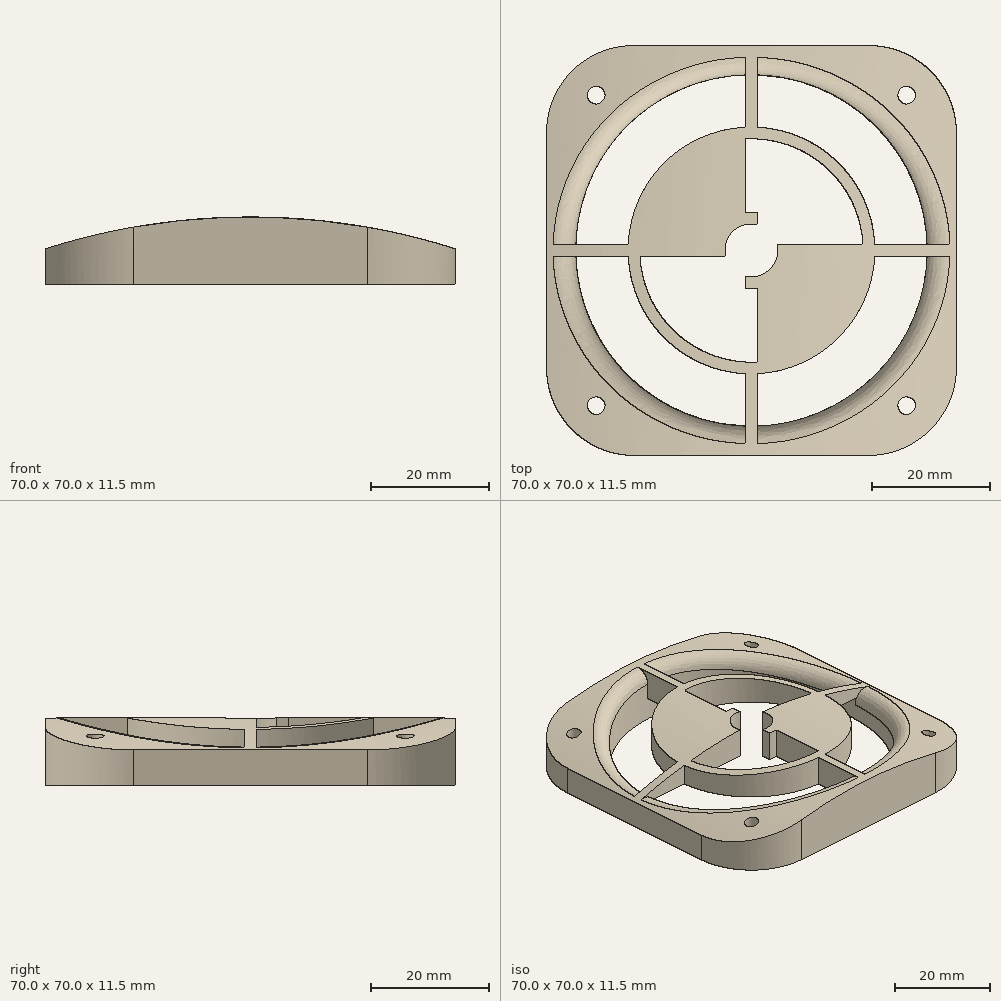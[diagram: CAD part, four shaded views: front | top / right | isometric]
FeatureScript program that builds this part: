
annotation { "Feature Type Name" : "Feature", "Feature Type Description" : "" }
export const myFeature = defineFeature(function(context is Context, id is Id, definition is map)
    precondition{}
    {
        {
            var Q0;
            Q0=qCreatedBy(makeId("Top.planeOp"),FACE);
            var sketch = newSketch(context, id + "F0", { "sketchPlane" : qUnion([Q0])});
            skLineSegment(sketch, "E0", {"start": v(0, 70.57) * mm, "end": v(0, -91.76) * mm, "construction": true});
            skLineSegment(sketch, "E1", {"start": v(-109.37, 0) * mm, "end": v(112.01, 0) * mm, "construction": true});
            skCircle(sketch, "E2", {"center": v(0, 0) * mm, "radius": 30 * mm});
            skLineSegment(sketch, "E3.bottom", {"start": v(35, 35) * mm, "end": v(-35, 35) * mm});
            skLineSegment(sketch, "E3.top", {"start": v(35, -35) * mm, "end": v(-35, -35) * mm});
            skLineSegment(sketch, "E3.left", {"start": v(35, 35) * mm, "end": v(35, -35) * mm});
            skLineSegment(sketch, "E3.right", {"start": v(-35, 35) * mm, "end": v(-35, -35) * mm});
            skLineSegment(sketch, "E4.bottom", {"start": v(26.5, 26.5) * mm, "end": v(-26.5, 26.5) * mm, "construction": true});
            skLineSegment(sketch, "E4.top", {"start": v(26.5, -26.5) * mm, "end": v(-26.5, -26.5) * mm, "construction": true});
            skLineSegment(sketch, "E4.left", {"start": v(26.5, 26.5) * mm, "end": v(26.5, -26.5) * mm, "construction": true});
            skLineSegment(sketch, "E4.right", {"start": v(-26.5, 26.5) * mm, "end": v(-26.5, -26.5) * mm, "construction": true});
            skCircle(sketch, "E5", {"center": v(26.5, 26.5) * mm, "radius": 1.5 * mm});
            skCircle(sketch, "E6.MirrorC", {"center": v(-26.5, 26.5) * mm, "radius": 1.5 * mm});
            skCircle(sketch, "E7.MirrorC", {"center": v(26.5, -26.5) * mm, "radius": 1.5 * mm});
            skCircle(sketch, "E8.MirrorC", {"center": v(-26.5, -26.5) * mm, "radius": 1.5 * mm});
            skCircle(sketch, "E9", {"center": v(0, 0) * mm, "radius": 6.52 * mm});
            skCircle(sketch, "E10.0", {"center": v(0, 0) * mm, "radius": 4.52 * mm});
            skCircle(sketch, "E11", {"center": v(0, 0) * mm, "radius": 19.07 * mm});
            skCircle(sketch, "E12.0", {"center": v(0, 0) * mm, "radius": 21.07 * mm});
            skLineSegment(sketch, "E13", {"start": v(-29.98, -1) * mm, "end": v(29.98, -1) * mm});
            skLineSegment(sketch, "E14.MirrorCS", {"start": v(-29.98, 1) * mm, "end": v(29.98, 1) * mm});
            skLineSegment(sketch, "E15", {"start": v(1, 29.98) * mm, "end": v(1, -29.98) * mm});
            skLineSegment(sketch, "E16.MirrorCS", {"start": v(-1, 29.98) * mm, "end": v(-1, -29.98) * mm});
            skSolve(sketch);
        }
        {
            var Q0;
            Q0=qSketchRegion(id+"F0",true);
            var Q1;
            {var subQ0=sQuery(id+"F0.wireOp",EDGE,"E16.MirrorCS");var subQ1=sQuery(id+"F0.wireOp",EDGE,"E11");var subQ2=makeQuery(id+"F0.imprint","INTERSECT",VERTEX,{"disambiguationData":[OD(0.0)],"derivedFrom":[subQ1,subQ0]});Q1=makeQuery(id+"F0.imprint","IMPRINT",FACE,{"disambiguationData":[TD([[makeQuery(id+"F0.imprint","IMPRINT",EDGE,{"disambiguationData":[TD([[subQ2,-1.0]])],"derivedFrom":subQ1}),-1.0]])]});}
            var Q2;
            {var subQ0=sQuery(id+"F0.wireOp",EDGE,"E13");var subQ1=sQuery(id+"F0.wireOp",EDGE,"E2");var subQ2=makeQuery(id+"F0.imprint","INTERSECT",VERTEX,{"disambiguationData":[OD(0.0)],"derivedFrom":[subQ1,subQ0]});Q2=makeQuery(id+"F0.imprint","IMPRINT",FACE,{"disambiguationData":[TD([[makeQuery(id+"F0.imprint","IMPRINT",EDGE,{"disambiguationData":[TD([[subQ2,1.0]])],"derivedFrom":subQ1}),1.0]])]});}
            var Q3;
            {var subQ0=sQuery(id+"F0.wireOp",EDGE,"E13");var subQ1=sQuery(id+"F0.wireOp",EDGE,"E11");var subQ2=makeQuery(id+"F0.imprint","INTERSECT",VERTEX,{"disambiguationData":[OD(0.0)],"derivedFrom":[subQ1,subQ0]});Q3=makeQuery(id+"F0.imprint","IMPRINT",FACE,{"disambiguationData":[TD([[makeQuery(id+"F0.imprint","IMPRINT",EDGE,{"disambiguationData":[TD([[subQ2,-1.0]])],"derivedFrom":subQ1}),-1.0]])]});}
            var Q4;
            {var subQ0=sQuery(id+"F0.wireOp",EDGE,"E14.MirrorCS");var subQ1=sQuery(id+"F0.wireOp",EDGE,"E9");var subQ2=makeQuery(id+"F0.imprint","INTERSECT",VERTEX,{"disambiguationData":[OD(1.0)],"derivedFrom":[subQ1,subQ0]});Q4=makeQuery(id+"F0.imprint","IMPRINT",FACE,{"disambiguationData":[TD([[makeQuery(id+"F0.imprint","IMPRINT",EDGE,{"disambiguationData":[TD([[subQ2,-1.0]])],"derivedFrom":subQ1}),-1.0]])]});}
            var Q5;
            {var subQ0=sQuery(id+"F0.wireOp",EDGE,"E14.MirrorCS");var subQ1=sQuery(id+"F0.wireOp",EDGE,"E11");var subQ2=makeQuery(id+"F0.imprint","INTERSECT",VERTEX,{"disambiguationData":[OD(1.0)],"derivedFrom":[subQ1,subQ0]});Q5=makeQuery(id+"F0.imprint","IMPRINT",FACE,{"disambiguationData":[TD([[makeQuery(id+"F0.imprint","IMPRINT",EDGE,{"disambiguationData":[TD([[subQ2,-1.0]])],"derivedFrom":subQ1}),-1.0]])]});}
            var Q6;
            {var subQ0=sQuery(id+"F0.wireOp",EDGE,"E13");var subQ1=sQuery(id+"F0.wireOp",EDGE,"E9");var subQ2=makeQuery(id+"F0.imprint","INTERSECT",VERTEX,{"disambiguationData":[OD(0.0)],"derivedFrom":[subQ1,subQ0]});Q6=makeQuery(id+"F0.imprint","IMPRINT",FACE,{"disambiguationData":[TD([[makeQuery(id+"F0.imprint","IMPRINT",EDGE,{"disambiguationData":[TD([[subQ2,-1.0]])],"derivedFrom":subQ1}),1.0]])]});}
            var Q7;
            {var subQ0=sQuery(id+"F0.wireOp",EDGE,"E14.MirrorCS");var subQ1=sQuery(id+"F0.wireOp",EDGE,"E9");var subQ2=makeQuery(id+"F0.imprint","INTERSECT",VERTEX,{"disambiguationData":[OD(1.0)],"derivedFrom":[subQ1,subQ0]});Q7=makeQuery(id+"F0.imprint","IMPRINT",FACE,{"disambiguationData":[TD([[makeQuery(id+"F0.imprint","IMPRINT",EDGE,{"disambiguationData":[TD([[subQ2,-1.0]])],"derivedFrom":subQ1}),1.0]])]});}
            var Q8;
            {var subQ0=sQuery(id+"F0.wireOp",EDGE,"E16.MirrorCS");var subQ1=sQuery(id+"F0.wireOp",EDGE,"E9");var subQ2=makeQuery(id+"F0.imprint","INTERSECT",VERTEX,{"disambiguationData":[OD(0.0)],"derivedFrom":[subQ1,subQ0]});Q8=makeQuery(id+"F0.imprint","IMPRINT",FACE,{"disambiguationData":[TD([[makeQuery(id+"F0.imprint","IMPRINT",EDGE,{"disambiguationData":[TD([[subQ2,-1.0]])],"derivedFrom":subQ1}),1.0]])]});}
            var Q9;
            {var subQ0=sQuery(id+"F0.wireOp",EDGE,"E15");var subQ1=sQuery(id+"F0.wireOp",EDGE,"E9");var subQ2=makeQuery(id+"F0.imprint","INTERSECT",VERTEX,{"disambiguationData":[OD(0.0)],"derivedFrom":[subQ1,subQ0]});Q9=makeQuery(id+"F0.imprint","IMPRINT",FACE,{"disambiguationData":[TD([[makeQuery(id+"F0.imprint","IMPRINT",EDGE,{"disambiguationData":[TD([[subQ2,-1.0]])],"derivedFrom":subQ1}),1.0]])]});}
            var Q10;
            {var subQ0=sQuery(id+"F0.wireOp",EDGE,"E15");var subQ1=sQuery(id+"F0.wireOp",EDGE,"E9");var subQ2=makeQuery(id+"F0.imprint","INTERSECT",VERTEX,{"disambiguationData":[OD(0.0)],"derivedFrom":[subQ1,subQ0]});Q10=makeQuery(id+"F0.imprint","IMPRINT",FACE,{"disambiguationData":[TD([[makeQuery(id+"F0.imprint","IMPRINT",EDGE,{"disambiguationData":[TD([[subQ2,1.0]])],"derivedFrom":subQ1}),1.0]])]});}
            var Q11;
            {var subQ0=sQuery(id+"F0.wireOp",EDGE,"E14.MirrorCS");var subQ1=sQuery(id+"F0.wireOp",EDGE,"E9");var subQ2=makeQuery(id+"F0.imprint","INTERSECT",VERTEX,{"disambiguationData":[OD(0.0)],"derivedFrom":[subQ1,subQ0]});Q11=makeQuery(id+"F0.imprint","IMPRINT",FACE,{"disambiguationData":[TD([[makeQuery(id+"F0.imprint","IMPRINT",EDGE,{"disambiguationData":[TD([[subQ2,1.0]])],"derivedFrom":subQ1}),1.0]])]});}
            var Q12;
            {var subQ0=sQuery(id+"F0.wireOp",EDGE,"E15");var subQ1=sQuery(id+"F0.wireOp",EDGE,"E9");var subQ2=makeQuery(id+"F0.imprint","INTERSECT",VERTEX,{"disambiguationData":[OD(1.0)],"derivedFrom":[subQ1,subQ0]});Q12=makeQuery(id+"F0.imprint","IMPRINT",FACE,{"disambiguationData":[TD([[makeQuery(id+"F0.imprint","IMPRINT",EDGE,{"disambiguationData":[TD([[subQ2,-1.0]])],"derivedFrom":subQ1}),1.0]])]});}
            var Q13;
            {var subQ0=sQuery(id+"F0.wireOp",EDGE,"E16.MirrorCS");var subQ1=sQuery(id+"F0.wireOp",EDGE,"E11");var subQ2=makeQuery(id+"F0.imprint","INTERSECT",VERTEX,{"disambiguationData":[OD(1.0)],"derivedFrom":[subQ1,subQ0]});Q13=makeQuery(id+"F0.imprint","IMPRINT",FACE,{"disambiguationData":[TD([[makeQuery(id+"F0.imprint","IMPRINT",EDGE,{"disambiguationData":[TD([[subQ2,-1.0]])],"derivedFrom":subQ1}),-1.0]])]});}
            var Q14;
            {var subQ0=sQuery(id+"F0.wireOp",EDGE,"E15");var subQ1=sQuery(id+"F0.wireOp",EDGE,"E2");var subQ2=makeQuery(id+"F0.imprint","INTERSECT",VERTEX,{"disambiguationData":[OD(1.0)],"derivedFrom":[subQ1,subQ0]});Q14=makeQuery(id+"F0.imprint","IMPRINT",FACE,{"disambiguationData":[TD([[makeQuery(id+"F0.imprint","IMPRINT",EDGE,{"disambiguationData":[TD([[subQ2,1.0]])],"derivedFrom":subQ1}),1.0]])]});}
            var Q15;
            {var subQ0=sQuery(id+"F0.wireOp",EDGE,"E16.MirrorCS");var subQ1=sQuery(id+"F0.wireOp",EDGE,"E9");var subQ2=makeQuery(id+"F0.imprint","INTERSECT",VERTEX,{"disambiguationData":[OD(1.0)],"derivedFrom":[subQ1,subQ0]});Q15=makeQuery(id+"F0.imprint","IMPRINT",FACE,{"disambiguationData":[TD([[makeQuery(id+"F0.imprint","IMPRINT",EDGE,{"disambiguationData":[TD([[subQ2,-1.0]])],"derivedFrom":subQ1}),-1.0]])]});}
            var Q16;
            {var subQ0=sQuery(id+"F0.wireOp",EDGE,"E15");var subQ1=sQuery(id+"F0.wireOp",EDGE,"E11");var subQ2=makeQuery(id+"F0.imprint","INTERSECT",VERTEX,{"disambiguationData":[OD(1.0)],"derivedFrom":[subQ1,subQ0]});Q16=makeQuery(id+"F0.imprint","IMPRINT",FACE,{"disambiguationData":[TD([[makeQuery(id+"F0.imprint","IMPRINT",EDGE,{"disambiguationData":[TD([[subQ2,-1.0]])],"derivedFrom":subQ1}),-1.0]])]});}
            var Q17;
            {var subQ0=sQuery(id+"F0.wireOp",EDGE,"E14.MirrorCS");var subQ1=sQuery(id+"F0.wireOp",EDGE,"E11");var subQ2=makeQuery(id+"F0.imprint","INTERSECT",VERTEX,{"disambiguationData":[OD(0.0)],"derivedFrom":[subQ1,subQ0]});Q17=makeQuery(id+"F0.imprint","IMPRINT",FACE,{"disambiguationData":[TD([[makeQuery(id+"F0.imprint","IMPRINT",EDGE,{"disambiguationData":[TD([[subQ2,1.0]])],"derivedFrom":subQ1}),-1.0]])]});}
            var Q18;
            {var subQ0=sQuery(id+"F0.wireOp",EDGE,"E14.MirrorCS");var subQ1=sQuery(id+"F0.wireOp",EDGE,"E9");var subQ2=makeQuery(id+"F0.imprint","INTERSECT",VERTEX,{"disambiguationData":[OD(0.0)],"derivedFrom":[subQ1,subQ0]});Q18=makeQuery(id+"F0.imprint","IMPRINT",FACE,{"disambiguationData":[TD([[makeQuery(id+"F0.imprint","IMPRINT",EDGE,{"disambiguationData":[TD([[subQ2,1.0]])],"derivedFrom":subQ1}),-1.0]])]});}
            var Q19;
            {var subQ0=sQuery(id+"F0.wireOp",EDGE,"E15");var subQ1=sQuery(id+"F0.wireOp",EDGE,"E11");var subQ2=makeQuery(id+"F0.imprint","INTERSECT",VERTEX,{"disambiguationData":[OD(0.0)],"derivedFrom":[subQ1,subQ0]});Q19=makeQuery(id+"F0.imprint","IMPRINT",FACE,{"disambiguationData":[TD([[makeQuery(id+"F0.imprint","IMPRINT",EDGE,{"disambiguationData":[TD([[subQ2,1.0]])],"derivedFrom":subQ1}),-1.0]])]});}
            var Q20;
            {var subQ0=sQuery(id+"F0.wireOp",EDGE,"E15");var subQ1=sQuery(id+"F0.wireOp",EDGE,"E11");var subQ2=makeQuery(id+"F0.imprint","INTERSECT",VERTEX,{"disambiguationData":[OD(0.0)],"derivedFrom":[subQ1,subQ0]});Q20=makeQuery(id+"F0.imprint","IMPRINT",FACE,{"disambiguationData":[TD([[makeQuery(id+"F0.imprint","IMPRINT",EDGE,{"disambiguationData":[TD([[subQ2,-1.0]])],"derivedFrom":subQ1}),-1.0]])]});}
            var Q21;
            {var subQ0=sQuery(id+"F0.wireOp",EDGE,"E15");var subQ1=sQuery(id+"F0.wireOp",EDGE,"E2");var subQ2=makeQuery(id+"F0.imprint","INTERSECT",VERTEX,{"disambiguationData":[OD(0.0)],"derivedFrom":[subQ1,subQ0]});Q21=makeQuery(id+"F0.imprint","IMPRINT",FACE,{"disambiguationData":[TD([[makeQuery(id+"F0.imprint","IMPRINT",EDGE,{"disambiguationData":[TD([[subQ2,-1.0]])],"derivedFrom":subQ1}),1.0]])]});}
            var Q22;
            {var subQ0=sQuery(id+"F0.wireOp",EDGE,"E15");var subQ1=sQuery(id+"F0.wireOp",EDGE,"E9");var subQ2=makeQuery(id+"F0.imprint","INTERSECT",VERTEX,{"disambiguationData":[OD(0.0)],"derivedFrom":[subQ1,subQ0]});Q22=makeQuery(id+"F0.imprint","IMPRINT",FACE,{"disambiguationData":[TD([[makeQuery(id+"F0.imprint","IMPRINT",EDGE,{"disambiguationData":[TD([[subQ2,-1.0]])],"derivedFrom":subQ1}),-1.0]])]});}
            var Q23;
            {var subQ0=sQuery(id+"F0.wireOp",EDGE,"E16.MirrorCS");var subQ1=sQuery(id+"F0.wireOp",EDGE,"E9");var subQ2=makeQuery(id+"F0.imprint","INTERSECT",VERTEX,{"disambiguationData":[OD(1.0)],"derivedFrom":[subQ1,subQ0]});Q23=makeQuery(id+"F0.imprint","IMPRINT",FACE,{"disambiguationData":[TD([[makeQuery(id+"F0.imprint","IMPRINT",EDGE,{"disambiguationData":[TD([[subQ2,-1.0]])],"derivedFrom":subQ1}),1.0]])]});}
            var Q24;
            {var subQ0=sQuery(id+"F0.wireOp",EDGE,"E13");var subQ1=sQuery(id+"F0.wireOp",EDGE,"E2");var subQ2=makeQuery(id+"F0.imprint","INTERSECT",VERTEX,{"disambiguationData":[OD(1.0)],"derivedFrom":[subQ1,subQ0]});Q24=makeQuery(id+"F0.imprint","IMPRINT",FACE,{"disambiguationData":[TD([[makeQuery(id+"F0.imprint","IMPRINT",EDGE,{"disambiguationData":[TD([[subQ2,-1.0]])],"derivedFrom":subQ1}),1.0]])]});}
            extrude(context, id + "F1", {"entities" : qUnion([Q0, Q1, Q2, Q3, Q4, Q5, Q6, Q7, Q8, Q9, Q10, Q11, Q12, Q13, Q14, Q15, Q16, Q17, Q18, Q19, Q20, Q21, Q22, Q23, Q24]), "depth" : 25 * mm, "offsetDistance" : 25 * mm});
        }
        {
            var Q0;
            Q0=makeQuery(id+"F1.opExtrude","SWEPT_FACE",FACE,{"disambiguationData":[OSD([sQuery(id+"F0.wireOp",EDGE,"E3.top")])]});
            var sketch = newSketch(context, id + "F2", { "sketchPlane" : qUnion([Q0])});
            skPoint(sketch, "E17", {"position": v(-35, 6) * mm});
            skPoint(sketch, "E18", {"position": v(35, 6) * mm});
            skCircle(sketch, "E19", {"center": v(0, -103.54) * mm, "radius": 115 * mm});
            skPoint(sketch, "E19.third.point", {"position": v(3.15, -218.5) * mm});
            skSolve(sketch);
        }
        {
            var Q0;
            {var subQ1=sQuery(id+"F0.wireOp",EDGE,"E3.top");var subQ6=makeQuery(id+"F1.opExtrude","CAP_EDGE",EDGE,{"disambiguationData":[OSD([subQ1])],"isStart":false});Q0=makeQuery(id+"F2.imprint","IMPRINT",FACE,{"disambiguationData":[TD([[makeQuery(id+"F2.imprint","IMPRINT",EDGE,{"derivedFrom":subQ6}),1.0]])]});}
            extrude(context, id + "F3", {"entities" : qUnion([Q0]), "operationType" : NewBodyOperationType.REMOVE, "oppositeDirection" : true, "depth" : 76 * mm});
        }
        {
            var Q0;
            Q0=makeQuery(id+"F1.opExtrude","SWEPT_EDGE",EDGE,{"disambiguationData":[OSD([sQuery(id+"F0.wireOp",EDGE,"E3.bottom"),sQuery(id+"F0.wireOp",EDGE,"E3.left")])]});
            var Q1;
            Q1=makeQuery(id+"F1.opExtrude","SWEPT_EDGE",EDGE,{"disambiguationData":[OSD([sQuery(id+"F0.wireOp",EDGE,"E3.top"),sQuery(id+"F0.wireOp",EDGE,"E3.left")])]});
            var Q2;
            Q2=makeQuery(id+"F1.opExtrude","SWEPT_EDGE",EDGE,{"disambiguationData":[OSD([sQuery(id+"F0.wireOp",EDGE,"E3.bottom"),sQuery(id+"F0.wireOp",EDGE,"E3.right")])]});
            var Q3;
            Q3=makeQuery(id+"F1.opExtrude","SWEPT_EDGE",EDGE,{"disambiguationData":[OSD([sQuery(id+"F0.wireOp",EDGE,"E3.top"),sQuery(id+"F0.wireOp",EDGE,"E3.right")])]});
            fillet(context, id + "F4", {"entities" : qUnion([Q0, Q1, Q2, Q3]), "radius" : 15 * mm, "tangentPropagation" : true, "allowEdgeOverflow" : false});
        }
        {
            var Q0;
            Q0=makeQuery(id+"F3.boolean.opBoolean","INTERSECT",EDGE,{"derivedFrom":[makeQuery(id+"F1.opExtrude","SWEPT_FACE",FACE,{"disambiguationData":[OSD([sQuery(id+"F0.wireOp",EDGE,"E2")])]}),makeQuery(id+"F3.opExtrude","SWEPT_FACE",FACE,{"disambiguationData":[OSD([sQuery(id+"F2.wireOp",EDGE,"E19")])]})]});
            fillet(context, id + "F5", {"entities" : qUnion([Q0]), "radius" : 3 * mm, "tangentPropagation" : true, "allowEdgeOverflow" : false});
        }
        {
            var Q0;
            Q0=makeQuery(id+"F1.opExtrude","CAP_FACE",FACE,{"disambiguationData":[OSD([sQuery(id+"F0.wireOp",EDGE,"E2"),sQuery(id+"F0.wireOp",EDGE,"E3.bottom"),sQuery(id+"F0.wireOp",EDGE,"E3.top"),sQuery(id+"F0.wireOp",EDGE,"E3.left"),sQuery(id+"F0.wireOp",EDGE,"E3.right"),sQuery(id+"F0.wireOp",EDGE,"E5"),sQuery(id+"F0.wireOp",EDGE,"E6.MirrorC"),sQuery(id+"F0.wireOp",EDGE,"E7.MirrorC"),sQuery(id+"F0.wireOp",EDGE,"E8.MirrorC"),sQuery(id+"F0.wireOp",EDGE,"E9"),sQuery(id+"F0.wireOp",EDGE,"E10.0"),sQuery(id+"F0.wireOp",EDGE,"E11"),sQuery(id+"F0.wireOp",EDGE,"E12.0"),sQuery(id+"F0.wireOp",EDGE,"E13"),sQuery(id+"F0.wireOp",EDGE,"E14.MirrorCS"),sQuery(id+"F0.wireOp",EDGE,"E15"),sQuery(id+"F0.wireOp",EDGE,"E16.MirrorCS")])],"isStart":true});
            var sketch = newSketch(context, id + "F6", { "sketchPlane" : qUnion([Q0])});
            skCircle(sketch, "E20", {"center": v(0, 0) * mm, "radius": 30 * mm});
            skSolve(sketch);
        }
        {
            var Q0;
            Q0=qSketchRegion(id+"F6",true);
            extrude(context, id + "F7", {"entities" : qUnion([Q0]), "operationType" : NewBodyOperationType.REMOVE, "oppositeDirection" : true, "depth" : 5 * mm});
        }
    });
